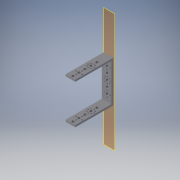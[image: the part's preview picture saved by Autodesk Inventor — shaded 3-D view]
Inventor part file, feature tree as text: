
AUTODESK INVENTOR PART (.ipt)
format: ipt  version: 2016 (Build 200138000, 138)  size: 278,016 bytes
history: native  units: in
note: dims shown in document units (in); Inventor stores cm internally (conversion verified against a paired STEP export)
features: reference x8, sketch x6, extrude x5, plane x2
ambient origin geometry x8: Origin, YZ Plane, XZ Plane, XY Plane, X Axis, Y Axis, Z Axis, Center Point
bodies: Solid1 (feature_tree)
feature tree (21):
  plane  "Work Plane1"
  extrude  "Extrusion1"  Depth=0.193in
  plane  "Work Plane2"
  extrude  "Extrusion2"  Depth=0.193in TaperAngle=0.0deg
  sketch  "Sketch3"  dims[d6=0.818in d7=0.0in d8=0.807in d9=0.0in]
  extrude  "Extrusion3"  Depth=0.807in TaperAngle=0.0deg
  extrude  "Extrusion4"  [1 undecoded]
  extrude  "Extrusion5"  [1 undecoded]
  sketch  "Sketch1"  dims[d0=0.193in d1=0.193in]
  sketch  "Sketch2"  dims[d2=4.0in d3=0.0in d4=0.193in d5=0.0in]
  reference  "Reference1"
  reference  "Reference2"
  reference  "Reference3"
  reference  "Reference4"
  reference  "Reference5"
  sketch  "Sketch4"  dims[d10=1.443in d11=0.0in]
  reference  "Reference6"
  sketch  "Sketch5"
  reference  "Reference7"
  sketch  "Sketch6"
  reference  "Reference8"
note: 2 required parameter values undecoded (feature->parameter linkage not recoverable at this tier; creation-order binding heuristic only, values carry confidence <= 0.55)
